# Revit family: Anchor Bolts Hook-Side
name_source: partatom
category: Detail Items
revit_build: Autodesk Revit Architecture 2012 (Build: 20110210_1515)
units: mm (PartAtom-declared; Revit-internal decimal feet)

## types (8) — shared parameters
Embedment = 0' - 6"

## per-type parameters (varying)
| type | Bend Radius Inside | Bend Radius Outside | Diameter | F3 | H diff | H1 | Head Height | Head Width | Keynote | Washer Height |
| 1 1/2" | 0' - 3" | 0' - 4 1/2" | 0' - 1 1/2" | 0' - 0 23/32" | 0' - 0 3/16" | 0' - 0 3/4" | 0' - 0 15/16" | 0' - 2 27/32" | 05 05 23.E8 | 0' - 0 3/32" |
| 3/4" | 0' - 1 1/2" | 0' - 2 1/4" | 0' - 0 3/4" | 0' - 0 11/32" | 0' - 0 3/32" | 0' - 0 3/8" | 0' - 0 15/32" | 0' - 1 13/32" | 05 05 23.E4 | 0' - 0 1/16" |
| 1 1/4" | 0' - 2 1/2" | 0' - 3 3/4" | 0' - 1 1/4" | 0' - 0 19/32" | 0' - 0 5/32" | 0' - 0 5/8" | 0' - 0 25/32" | 0' - 2 11/32" | 05 05 23.E7 | 0' - 0 3/32" |
| 1" | 0' - 2" | 0' - 3" | 0' - 1" | 0' - 0 15/32" | 0' - 0 1/8" | 0' - 0 1/2" | 0' - 0 5/8" | 0' - 1 7/8" | 05 05 23.E6 | 0' - 0 1/16" |
| 1/2" | 0' - 1" | 0' - 1 1/2" | 0' - 0 1/2" | 0' - 0 1/4" | 0' - 0 1/16" | 0' - 0 1/4" | 0' - 0 5/16" | 0' - 0 15/16" | 05 05 23.E2 | 0' - 0 1/32" |
| 3/8" | 0' - 0 3/4" | 0' - 1 1/8" | 0' - 0 3/8" | 0' - 0 3/16" | 0' - 0 1/32" | 0' - 0 3/16" | 0' - 0 7/32" | 0' - 0 11/16" | 05 05 23.E1 | 0' - 0 1/32" |
| 5/8" | 0' - 1 1/4" | 0' - 1 7/8" | 0' - 0 5/8" | 0' - 0 9/32" | 0' - 0 3/32" | 0' - 0 5/16" | 0' - 0 13/32" | 0' - 1 3/16" | 05 05 23.E3 | 0' - 0 1/32" |
| 7/8" | 0' - 1 3/4" | 0' - 2 5/8" | 0' - 0 7/8" | 0' - 0 13/32" | 0' - 0 1/8" | 0' - 0 7/16" | 0' - 0 9/16" | 0' - 1 21/32" | 05 05 23.E5 | 0' - 0 1/16" |
